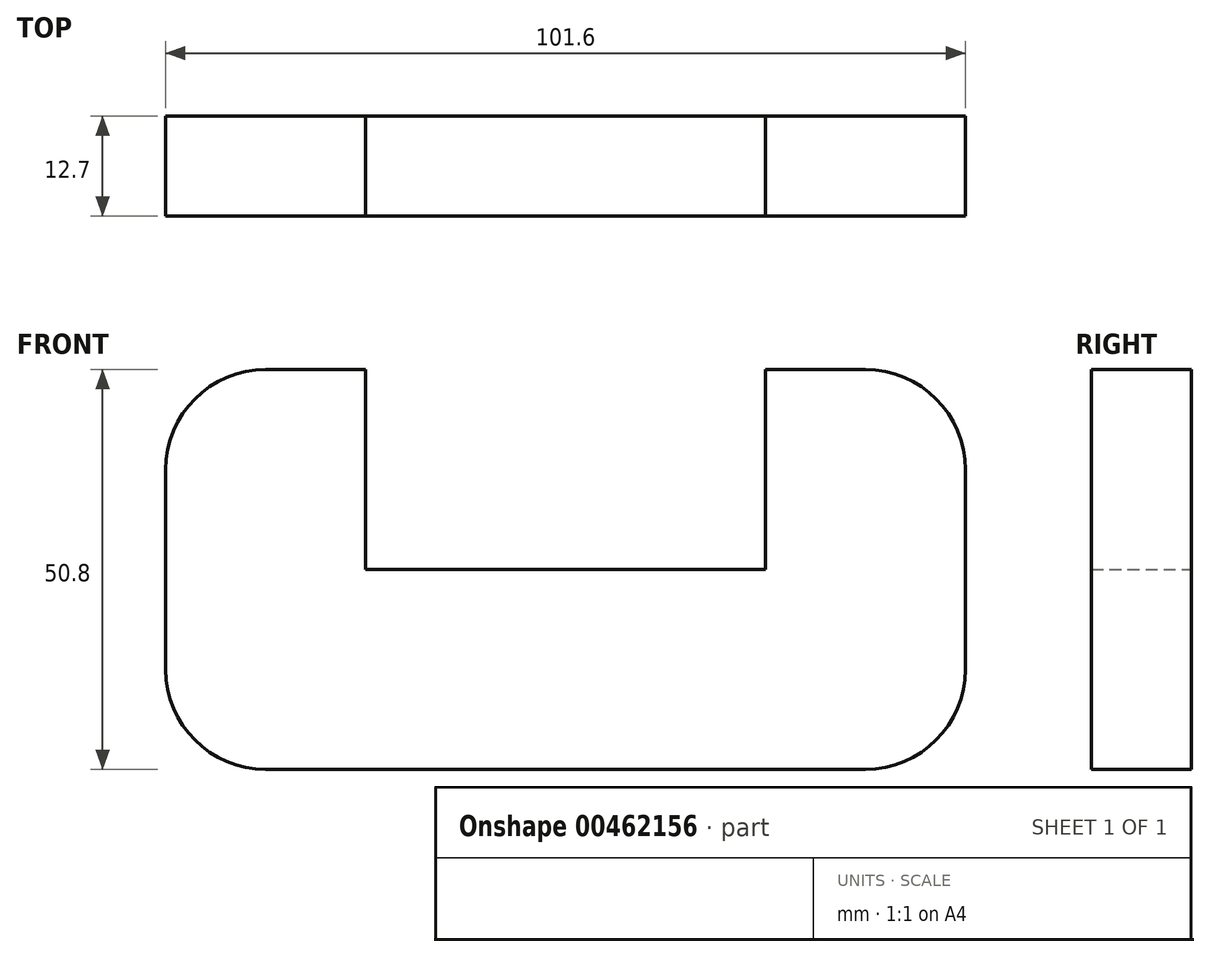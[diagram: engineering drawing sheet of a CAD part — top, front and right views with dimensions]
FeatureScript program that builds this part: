
annotation { "Feature Type Name" : "Feature", "Feature Type Description" : "" }
export const myFeature = defineFeature(function(context is Context, id is Id, definition is map)
    precondition{}
    {
        {
            var Q0;
            Q0=qCreatedBy(makeId("Front.planeOp"),FACE);
            var sketch = newSketch(context, id + "F0", { "sketchPlane" : qUnion([Q0])});
            skLineSegment(sketch, "E0.bottom", {"start": v(38.1, -25.4) * mm, "end": v(-38.1, -25.4) * mm});
            skLineSegment(sketch, "E0.top", {"start": v(38.1, 25.4) * mm, "end": v(-38.1, 25.4) * mm});
            skLineSegment(sketch, "E0.left", {"start": v(50.8, -12.7) * mm, "end": v(50.8, 12.7) * mm});
            skLineSegment(sketch, "E0.right", {"start": v(-50.8, -12.7) * mm, "end": v(-50.8, 12.7) * mm});
            skPoint(sketch, "E0.middle", {"position": v(0, 0) * mm});
            skLineSegment(sketch, "E1.bottom", {"start": v(-25.4, 25.4) * mm, "end": v(25.4, 25.4) * mm});
            skLineSegment(sketch, "E1.top", {"start": v(-25.4, 0) * mm, "end": v(25.4, 0) * mm});
            skLineSegment(sketch, "E1.left", {"start": v(-25.4, 25.4) * mm, "end": v(-25.4, 0) * mm});
            skLineSegment(sketch, "E1.right", {"start": v(25.4, 25.4) * mm, "end": v(25.4, 0) * mm});
            skPoint(sketch, "E2.visualSharp", {"position": v(-50.8, -25.4) * mm});
            skArc(sketch, "E2.filletArc", {"start": v(-50.8, -12.7) * mm, "mid": v(-47.08, -21.68) * mm, "end": v(-38.1, -25.4) * mm});
            skPoint(sketch, "E3.visualSharp", {"position": v(50.8, -25.4) * mm});
            skArc(sketch, "E3.filletArc", {"start": v(38.1, -25.4) * mm, "mid": v(47.08, -21.68) * mm, "end": v(50.8, -12.7) * mm});
            skPoint(sketch, "E4.visualSharp", {"position": v(50.8, 25.4) * mm});
            skArc(sketch, "E4.filletArc", {"start": v(50.8, 12.7) * mm, "mid": v(47.08, 21.68) * mm, "end": v(38.1, 25.4) * mm});
            skPoint(sketch, "E5.visualSharp", {"position": v(-50.8, 25.4) * mm});
            skArc(sketch, "E5.filletArc", {"start": v(-38.1, 25.4) * mm, "mid": v(-47.08, 21.68) * mm, "end": v(-50.8, 12.7) * mm});
            skSolve(sketch);
        }
        {
            var Q0;
            Q0=makeQuery(id+"F0.imprint","IMPRINT",FACE,{"disambiguationData":[TD([[makeQuery(id+"F0.imprint","IMPRINT",EDGE,{"derivedFrom":sQuery(id+"F0.wireOp",EDGE,"E0.bottom")}),-1.0]])]});
            extrude(context, id + "F1", {"entities" : qUnion([Q0]), "depth" : 12.7 * mm, "symmetric" : true});
        }
    });
